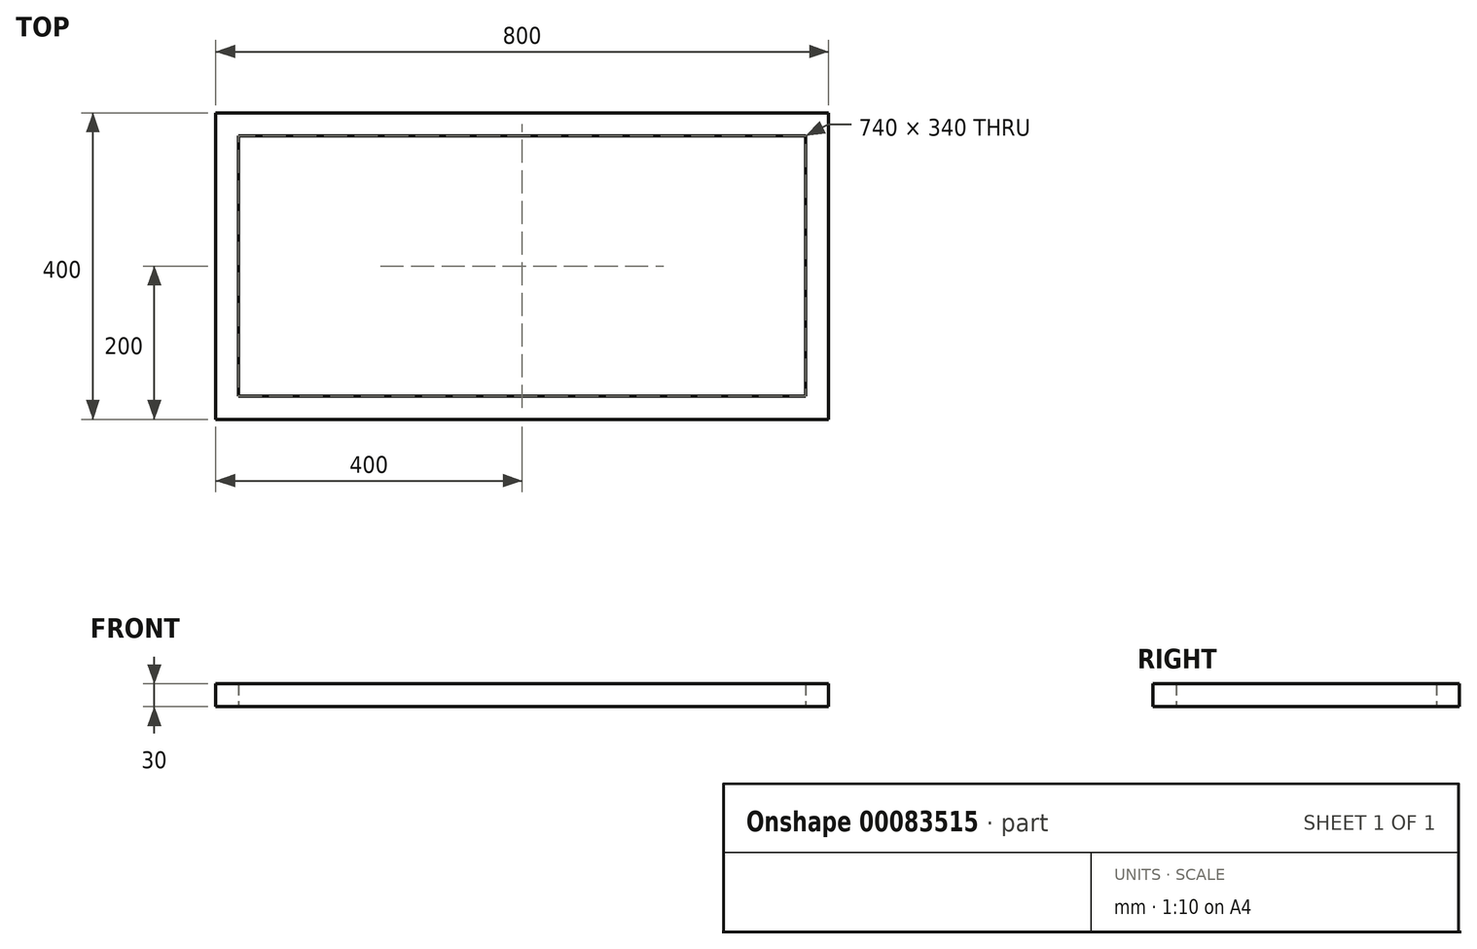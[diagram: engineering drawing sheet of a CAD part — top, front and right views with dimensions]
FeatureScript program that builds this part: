
annotation { "Feature Type Name" : "Feature", "Feature Type Description" : "" }
export const myFeature = defineFeature(function(context is Context, id is Id, definition is map)
    precondition{}
    {
        {
            var Q0;
            Q0=qCreatedBy(makeId("Top.planeOp"),FACE);
            var sketch = newSketch(context, id + "F0", { "sketchPlane" : qUnion([Q0])});
            skLineSegment(sketch, "E0.bottom", {"start": v(-400, 200) * mm, "end": v(400, 200) * mm});
            skLineSegment(sketch, "E0.top", {"start": v(-400, -200) * mm, "end": v(400, -200) * mm});
            skLineSegment(sketch, "E0.left", {"start": v(-400, 200) * mm, "end": v(-400, -200) * mm});
            skLineSegment(sketch, "E0.right", {"start": v(400, 200) * mm, "end": v(400, -200) * mm});
            skPoint(sketch, "E0.middle", {"position": v(0, 0) * mm});
            skLineSegment(sketch, "E1.0", {"start": v(-370, 170) * mm, "end": v(370, 170) * mm});
            skLineSegment(sketch, "E1.1", {"start": v(-370, 170) * mm, "end": v(-370, -170) * mm});
            skLineSegment(sketch, "E1.2", {"start": v(-370, -170) * mm, "end": v(370, -170) * mm});
            skLineSegment(sketch, "E1.3", {"start": v(370, 170) * mm, "end": v(370, -170) * mm});
            skSolve(sketch);
        }
        {
            var Q0;
            Q0=makeQuery(id+"F0.imprint","IMPRINT",FACE,{"disambiguationData":[TD([[makeQuery(id+"F0.imprint","IMPRINT",EDGE,{"derivedFrom":sQuery(id+"F0.wireOp",EDGE,"E0.bottom")}),-1.0]])]});
            extrude(context, id + "F1", {"entities" : qUnion([Q0]), "depth" : 30 * mm});
        }
    });
